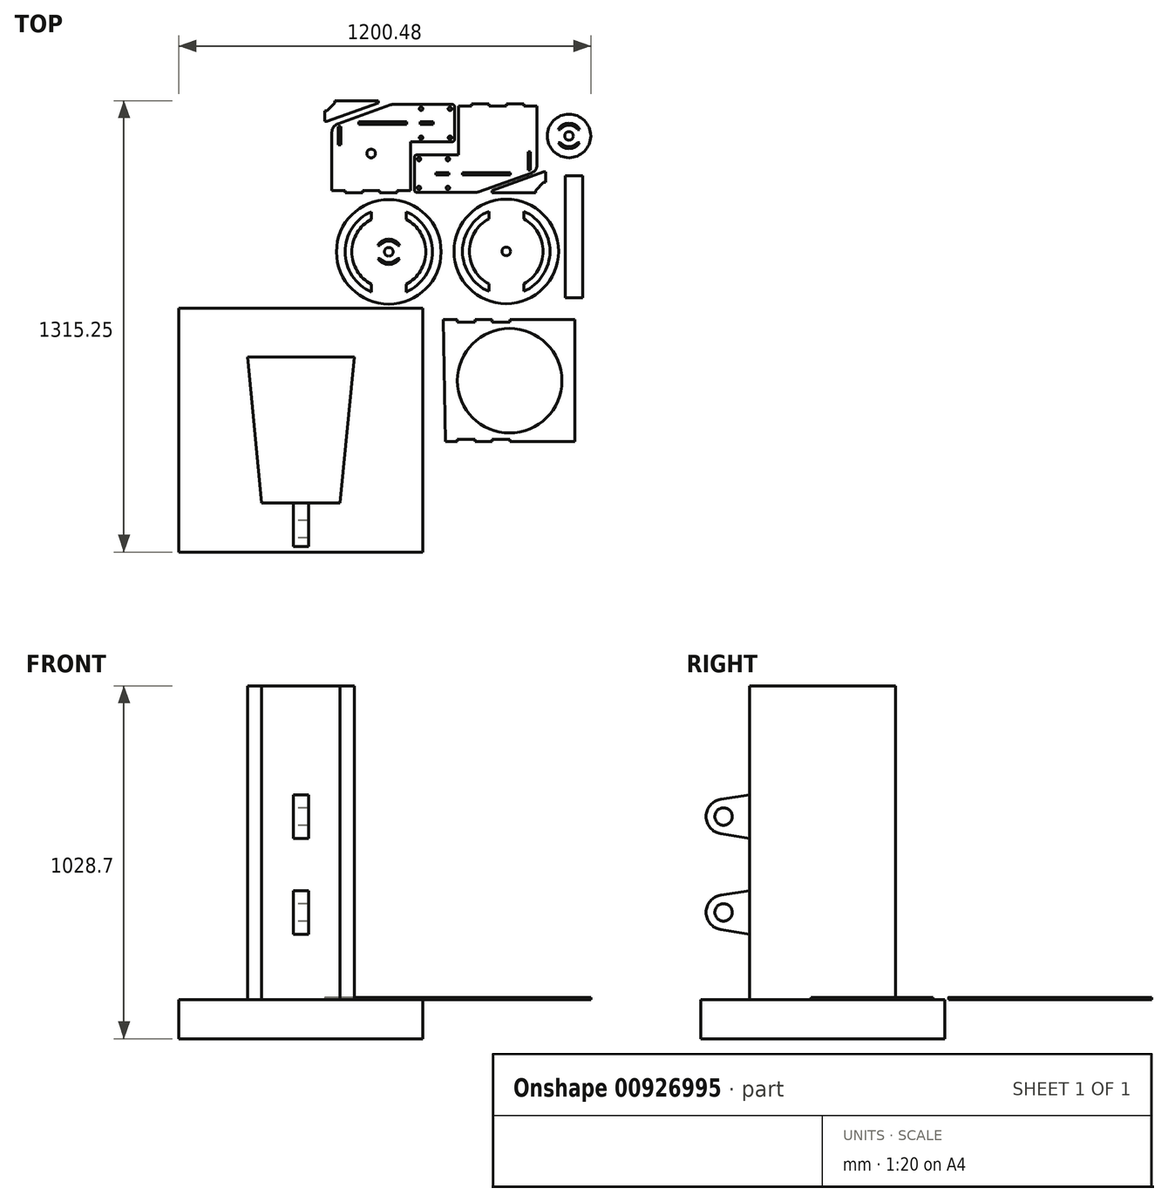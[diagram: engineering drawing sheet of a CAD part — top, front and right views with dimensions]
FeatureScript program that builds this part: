
annotation { "Feature Type Name" : "Feature", "Feature Type Description" : "" }
export const myFeature = defineFeature(function(context is Context, id is Id, definition is map)
    precondition{}
    {
        {
            var Q0;
            Q0=qCreatedBy(makeId("Top.planeOp"),FACE);
            var sketch = newSketch(context, id + "F0", { "sketchPlane" : qUnion([Q0])});
            skLineSegment(sketch, "E0", {"start": v(-368.3, -165.1) * mm, "end": v(0, -165.1) * mm});
            skLineSegment(sketch, "E1", {"start": v(101.6, -104.11) * mm, "end": v(101.6, -82.12) * mm});
            skArc(sketch, "E2", {"start": v(101.6, 107.52) * mm, "mid": v(44.83, 12.7) * mm, "end": v(101.6, -82.12) * mm});
            skArc(sketch, "E3", {"start": v(101.6, 129.51) * mm, "mid": v(25.02, 12.7) * mm, "end": v(101.6, -104.11) * mm});
            skLineSegment(sketch, "E4", {"start": v(-221.48, 30.45) * mm, "end": v(-214.81, 30.45) * mm});
            skLineSegment(sketch, "E5", {"start": v(-368.3, 190.5) * mm, "end": v(0, 190.5) * mm});
            skArc(sketch, "E6", {"start": v(-158.3, 30.45) * mm, "mid": v(-189.89, 48.3) * mm, "end": v(-221.48, 30.45) * mm});
            skLineSegment(sketch, "E7", {"start": v(0, 183.9) * mm, "end": v(52.07, 183.9) * mm});
            skLineSegment(sketch, "E8", {"start": v(52.07, 183.9) * mm, "end": v(52.07, 190.5) * mm});
            skLineSegment(sketch, "E9", {"start": v(52.07, 190.5) * mm, "end": v(101.6, 190.5) * mm});
            skLineSegment(sketch, "E10", {"start": v(101.6, 190.5) * mm, "end": v(101.6, 183.9) * mm});
            skLineSegment(sketch, "E11", {"start": v(101.6, 183.9) * mm, "end": v(153.67, 183.9) * mm});
            skLineSegment(sketch, "E12", {"start": v(153.67, 183.9) * mm, "end": v(153.67, 190.5) * mm});
            skLineSegment(sketch, "E13", {"start": v(153.67, 190.5) * mm, "end": v(342.9, 190.5) * mm});
            skLineSegment(sketch, "E14", {"start": v(52.07, -165.1) * mm, "end": v(101.6, -165.1) * mm});
            skLineSegment(sketch, "E15", {"start": v(153.67, -165.1) * mm, "end": v(342.9, -165.1) * mm});
            skCircle(sketch, "E16", {"center": v(-189.89, 11.4) * mm, "radius": 152.4 * mm});
            skLineSegment(sketch, "E17", {"start": v(0, 183.9) * mm, "end": v(0, 190.5) * mm});
            skLineSegment(sketch, "E18", {"start": v(101.6, 107.52) * mm, "end": v(101.6, 129.51) * mm});
            skLineSegment(sketch, "E19", {"start": v(342.9, 190.5) * mm, "end": v(342.9, -165.1) * mm});
            skLineSegment(sketch, "E20", {"start": v(153.67, -158.5) * mm, "end": v(153.67, -165.1) * mm});
            skLineSegment(sketch, "E21", {"start": v(101.6, -158.5) * mm, "end": v(153.67, -158.5) * mm});
            skCircle(sketch, "E22", {"center": v(152.4, 12.7) * mm, "radius": 12.7 * mm});
            skLineSegment(sketch, "E23", {"start": v(101.6, -165.1) * mm, "end": v(101.6, -158.5) * mm});
            skLineSegment(sketch, "E24", {"start": v(52.07, -158.5) * mm, "end": v(52.07, -165.1) * mm});
            skLineSegment(sketch, "E25", {"start": v(0, -158.5) * mm, "end": v(52.07, -158.5) * mm});
            skLineSegment(sketch, "E26", {"start": v(0, -165.1) * mm, "end": v(0, -158.5) * mm});
            skLineSegment(sketch, "E27", {"start": v(-164.97, -7.65) * mm, "end": v(-158.3, -7.65) * mm});
            skLineSegment(sketch, "E28", {"start": v(-164.97, 30.45) * mm, "end": v(-158.3, 30.45) * mm});
            skLineSegment(sketch, "E29", {"start": v(-368.3, 190.5) * mm, "end": v(-368.3, -165.1) * mm});
            skCircle(sketch, "E30", {"center": v(-189.89, 11.4) * mm, "radius": 12.7 * mm});
            skArc(sketch, "E31", {"start": v(-164.97, 30.45) * mm, "mid": v(-189.89, 42.77) * mm, "end": v(-214.81, 30.45) * mm});
            skLineSegment(sketch, "E32", {"start": v(-221.48, -7.65) * mm, "end": v(-214.81, -7.65) * mm});
            skLineSegment(sketch, "E33", {"start": v(-139.09, 106.22) * mm, "end": v(-139.09, 128.22) * mm});
            skArc(sketch, "E34", {"start": v(-221.48, -7.65) * mm, "mid": v(-189.89, -25.5) * mm, "end": v(-158.3, -7.65) * mm});
            skArc(sketch, "E35", {"start": v(-240.69, 106.22) * mm, "mid": v(-297.46, 11.4) * mm, "end": v(-240.69, -83.42) * mm});
            skArc(sketch, "E36", {"start": v(-139.09, -83.42) * mm, "mid": v(-82.32, 11.4) * mm, "end": v(-139.09, 106.22) * mm});
            skArc(sketch, "E37", {"start": v(-240.69, 128.22) * mm, "mid": v(-317.27, 11.4) * mm, "end": v(-240.69, -105.41) * mm});
            skArc(sketch, "E38", {"start": v(-214.81, -7.65) * mm, "mid": v(-189.89, -19.97) * mm, "end": v(-164.97, -7.65) * mm});
            skLineSegment(sketch, "E39", {"start": v(-240.69, -105.41) * mm, "end": v(-240.69, -83.42) * mm});
            skLineSegment(sketch, "E40", {"start": v(-240.69, 106.22) * mm, "end": v(-240.69, 128.22) * mm});
            skLineSegment(sketch, "E41", {"start": v(-139.09, -105.41) * mm, "end": v(-139.09, -83.42) * mm});
            skCircle(sketch, "E42", {"center": v(152.4, 12.7) * mm, "radius": 152.4 * mm});
            skArc(sketch, "E43", {"start": v(-139.09, -105.41) * mm, "mid": v(-62.5, 11.4) * mm, "end": v(-139.09, 128.22) * mm});
            skLineSegment(sketch, "E44", {"start": v(203.2, 107.52) * mm, "end": v(203.2, 129.51) * mm});
            skArc(sketch, "E45", {"start": v(203.2, -82.12) * mm, "mid": v(259.97, 12.7) * mm, "end": v(203.2, 107.52) * mm});
            skArc(sketch, "E46", {"start": v(203.2, -104.11) * mm, "mid": v(279.78, 12.7) * mm, "end": v(203.2, 129.51) * mm});
            skLineSegment(sketch, "E47", {"start": v(203.2, -104.11) * mm, "end": v(203.2, -82.12) * mm});
            skSolve(sketch);
        }
        {
            var Q0;
            Q0=qCreatedBy(makeId("Top.planeOp"),FACE);
            var sketch = newSketch(context, id + "F1", { "sketchPlane" : qUnion([Q0])});
            skLineSegment(sketch, "E48", {"start": v(-119.77, 332.2) * mm, "end": v(-119.77, 441) * mm, "construction": true});
            skLineSegment(sketch, "E49", {"start": v(-336.68, 323) * mm, "end": v(-330.07, 323) * mm});
            skLineSegment(sketch, "E50", {"start": v(-336.68, 376.34) * mm, "end": v(-336.68, 323) * mm});
            skLineSegment(sketch, "E51", {"start": v(-330.07, 376.34) * mm, "end": v(-336.68, 376.34) * mm});
            skLineSegment(sketch, "E52", {"start": v(-330.07, 323) * mm, "end": v(-330.07, 376.34) * mm});
            skLineSegment(sketch, "E53", {"start": v(-277.47, 389.9) * mm, "end": v(-277.47, 383.3) * mm});
            skLineSegment(sketch, "E54", {"start": v(-137.77, 389.9) * mm, "end": v(-277.47, 389.9) * mm});
            skLineSegment(sketch, "E55", {"start": v(-137.77, 383.3) * mm, "end": v(-137.77, 389.9) * mm});
            skLineSegment(sketch, "E56", {"start": v(-277.47, 383.3) * mm, "end": v(-137.77, 383.3) * mm});
            skLineSegment(sketch, "E57", {"start": v(-127, 326.7) * mm, "end": v(-127, 190.18) * mm});
            skLineSegment(sketch, "E58", {"start": v(-127, 326.7) * mm, "end": v(-127, 332.2) * mm});
            skLineSegment(sketch, "E59", {"start": v(-127, 441) * mm, "end": v(-127, 332.2) * mm, "construction": true});
            skLineSegment(sketch, "E60", {"start": v(-176.58, 441) * mm, "end": v(-127, 441) * mm});
            skArc(sketch, "E61", {"start": v(-176.58, 441) * mm, "mid": v(-180.91, 440.64) * mm, "end": v(-185.11, 439.53) * mm});
            skLineSegment(sketch, "E62", {"start": v(-185.11, 439.53) * mm, "end": v(-338.73, 384.73) * mm});
            skArc(sketch, "E63", {"start": v(-338.73, 384.73) * mm, "mid": v(-350.96, 375.44) * mm, "end": v(-355.6, 360.8) * mm});
            skLineSegment(sketch, "E64", {"start": v(-355.6, 360.8) * mm, "end": v(-355.6, 190.18) * mm});
            skLineSegment(sketch, "E65", {"start": v(-317.5, 190.18) * mm, "end": v(-355.6, 190.18) * mm});
            skLineSegment(sketch, "E66", {"start": v(-317.5, 183.83) * mm, "end": v(-317.5, 190.18) * mm});
            skLineSegment(sketch, "E67", {"start": v(-317.5, 183.83) * mm, "end": v(-266.7, 183.83) * mm});
            skLineSegment(sketch, "E68", {"start": v(-266.7, 183.83) * mm, "end": v(-266.7, 190.18) * mm});
            skLineSegment(sketch, "E69", {"start": v(-266.7, 190.18) * mm, "end": v(-215.9, 190.18) * mm});
            skLineSegment(sketch, "E70", {"start": v(-215.9, 190.18) * mm, "end": v(-215.9, 183.83) * mm});
            skLineSegment(sketch, "E71", {"start": v(-215.9, 183.83) * mm, "end": v(-165.1, 183.83) * mm});
            skLineSegment(sketch, "E72", {"start": v(-165.1, 183.83) * mm, "end": v(-165.1, 190.18) * mm});
            skLineSegment(sketch, "E73", {"start": v(-165.1, 190.18) * mm, "end": v(-127, 190.18) * mm});
            skArc(sketch, "E74", {"start": v(-209.7, 317.18) * mm, "mid": v(-241.3, 335.03) * mm, "end": v(-272.9, 317.18) * mm});
            skLineSegment(sketch, "E75", {"start": v(-209.7, 317.18) * mm, "end": v(-216.38, 317.18) * mm});
            skArc(sketch, "E76", {"start": v(-216.38, 317.18) * mm, "mid": v(-241.3, 329.5) * mm, "end": v(-266.22, 317.18) * mm});
            skLineSegment(sketch, "E77", {"start": v(-266.22, 317.18) * mm, "end": v(-272.9, 317.18) * mm});
            skLineSegment(sketch, "E78", {"start": v(-266.22, 279.08) * mm, "end": v(-272.9, 279.08) * mm});
            skArc(sketch, "E79", {"start": v(-266.22, 279.08) * mm, "mid": v(-241.3, 266.76) * mm, "end": v(-216.38, 279.08) * mm});
            skLineSegment(sketch, "E80", {"start": v(-209.7, 279.08) * mm, "end": v(-216.38, 279.08) * mm});
            skArc(sketch, "E81", {"start": v(-272.9, 279.08) * mm, "mid": v(-241.3, 261.24) * mm, "end": v(-209.7, 279.08) * mm});
            skCircle(sketch, "E82", {"center": v(-241.3, 298.13) * mm, "radius": 12.7 * mm});
            skCircle(sketch, "E83", {"center": v(-11.6, 344.14) * mm, "radius": 5.08 * mm});
            skCircle(sketch, "E84", {"center": v(-11.6, 428.22) * mm, "radius": 5.08 * mm});
            skCircle(sketch, "E85", {"center": v(-95.68, 344.14) * mm, "radius": 5.08 * mm});
            skCircle(sketch, "E86", {"center": v(-95.68, 428.22) * mm, "radius": 5.08 * mm});
            skLineSegment(sketch, "E87", {"start": v(-112.54, 332.2) * mm, "end": v(-4.59, 332.2) * mm});
            skArc(sketch, "E88", {"start": v(-4.59, 332.2) * mm, "mid": v(-0.1, 334.07) * mm, "end": v(1.76, 338.56) * mm});
            skLineSegment(sketch, "E89", {"start": v(1.76, 338.56) * mm, "end": v(1.76, 434.66) * mm});
            skArc(sketch, "E90", {"start": v(1.76, 434.66) * mm, "mid": v(-0.1, 439.15) * mm, "end": v(-4.59, 441) * mm});
            skLineSegment(sketch, "E91", {"start": v(-4.59, 441) * mm, "end": v(-112.54, 441) * mm});
            skLineSegment(sketch, "E92", {"start": v(-112.54, 332.2) * mm, "end": v(-112.54, 441) * mm, "construction": true});
            skLineSegment(sketch, "E93", {"start": v(-60.74, 383.3) * mm, "end": v(-60.74, 389.9) * mm});
            skLineSegment(sketch, "E94", {"start": v(-98.84, 383.3) * mm, "end": v(-60.74, 383.3) * mm});
            skLineSegment(sketch, "E95", {"start": v(-98.84, 389.9) * mm, "end": v(-98.84, 383.3) * mm});
            skLineSegment(sketch, "E96", {"start": v(-60.74, 389.9) * mm, "end": v(-98.84, 389.9) * mm});
            skLineSegment(sketch, "E97", {"start": v(-127, 332.2) * mm, "end": v(-112.54, 332.2) * mm});
            skLineSegment(sketch, "E98", {"start": v(-112.54, 441) * mm, "end": v(-127, 441) * mm});
            skCircle(sketch, "E99", {"center": v(-241.3, 298.13) * mm, "radius": 63.5 * mm});
            skSolve(sketch);
        }
        {
            var Q0;
            Q0=qCreatedBy(makeId("Top.planeOp"),FACE);
            var sketch = newSketch(context, id + "F2", { "sketchPlane" : qUnion([Q0])});
            skLineSegment(sketch, "E100", {"start": v(6.33, 293.6) * mm, "end": v(6.33, 184.8) * mm, "construction": true});
            skLineSegment(sketch, "E101", {"start": v(223.24, 302.8) * mm, "end": v(216.63, 302.8) * mm});
            skLineSegment(sketch, "E102", {"start": v(223.24, 249.47) * mm, "end": v(223.24, 302.8) * mm});
            skLineSegment(sketch, "E103", {"start": v(216.63, 249.47) * mm, "end": v(223.24, 249.47) * mm});
            skLineSegment(sketch, "E104", {"start": v(216.63, 302.8) * mm, "end": v(216.63, 249.47) * mm});
            skLineSegment(sketch, "E105", {"start": v(164.04, 235.9) * mm, "end": v(164.04, 242.5) * mm});
            skLineSegment(sketch, "E106", {"start": v(24.34, 235.9) * mm, "end": v(164.04, 235.9) * mm});
            skLineSegment(sketch, "E107", {"start": v(24.34, 242.5) * mm, "end": v(24.34, 235.9) * mm});
            skLineSegment(sketch, "E108", {"start": v(164.04, 242.5) * mm, "end": v(24.34, 242.5) * mm});
            skLineSegment(sketch, "E109", {"start": v(13.56, 299.1) * mm, "end": v(13.56, 435.63) * mm});
            skLineSegment(sketch, "E110", {"start": v(13.56, 299.1) * mm, "end": v(13.56, 293.6) * mm});
            skLineSegment(sketch, "E111", {"start": v(13.56, 184.8) * mm, "end": v(13.56, 293.6) * mm, "construction": true});
            skLineSegment(sketch, "E112", {"start": v(63.14, 184.8) * mm, "end": v(13.56, 184.8) * mm});
            skArc(sketch, "E113", {"start": v(63.14, 184.8) * mm, "mid": v(67.47, 185.18) * mm, "end": v(71.68, 186.28) * mm});
            skLineSegment(sketch, "E114", {"start": v(71.68, 186.28) * mm, "end": v(225.3, 241.08) * mm});
            skArc(sketch, "E115", {"start": v(225.3, 241.08) * mm, "mid": v(237.52, 250.37) * mm, "end": v(242.16, 265) * mm});
            skLineSegment(sketch, "E116", {"start": v(242.16, 265) * mm, "end": v(242.16, 435.63) * mm});
            skLineSegment(sketch, "E117", {"start": v(204.06, 435.63) * mm, "end": v(242.16, 435.63) * mm});
            skLineSegment(sketch, "E118", {"start": v(204.06, 441.98) * mm, "end": v(204.06, 435.63) * mm});
            skLineSegment(sketch, "E119", {"start": v(204.06, 441.98) * mm, "end": v(153.26, 441.98) * mm});
            skLineSegment(sketch, "E120", {"start": v(153.26, 441.98) * mm, "end": v(153.26, 435.63) * mm});
            skLineSegment(sketch, "E121", {"start": v(153.26, 435.63) * mm, "end": v(102.46, 435.63) * mm});
            skLineSegment(sketch, "E122", {"start": v(102.46, 435.63) * mm, "end": v(102.46, 441.98) * mm});
            skLineSegment(sketch, "E123", {"start": v(102.46, 441.98) * mm, "end": v(51.66, 441.98) * mm});
            skLineSegment(sketch, "E124", {"start": v(51.66, 441.98) * mm, "end": v(51.66, 435.63) * mm});
            skLineSegment(sketch, "E125", {"start": v(51.66, 435.63) * mm, "end": v(13.56, 435.63) * mm});
            skCircle(sketch, "E126", {"center": v(-101.84, 281.67) * mm, "radius": 5.08 * mm});
            skCircle(sketch, "E127", {"center": v(-101.84, 197.6) * mm, "radius": 5.08 * mm});
            skCircle(sketch, "E128", {"center": v(-17.76, 281.67) * mm, "radius": 5.08 * mm});
            skCircle(sketch, "E129", {"center": v(-17.76, 197.6) * mm, "radius": 5.08 * mm});
            skLineSegment(sketch, "E130", {"start": v(-0.9, 293.6) * mm, "end": v(-108.85, 293.6) * mm});
            skArc(sketch, "E131", {"start": v(-108.85, 293.6) * mm, "mid": v(-113.34, 291.75) * mm, "end": v(-115.2, 287.26) * mm});
            skLineSegment(sketch, "E132", {"start": v(-115.2, 287.26) * mm, "end": v(-115.2, 191.15) * mm});
            skArc(sketch, "E133", {"start": v(-115.2, 191.15) * mm, "mid": v(-113.34, 186.66) * mm, "end": v(-108.85, 184.8) * mm});
            skLineSegment(sketch, "E134", {"start": v(-108.85, 184.8) * mm, "end": v(-0.9, 184.8) * mm});
            skLineSegment(sketch, "E135", {"start": v(-0.9, 293.6) * mm, "end": v(-0.9, 184.8) * mm, "construction": true});
            skLineSegment(sketch, "E136", {"start": v(-52.7, 242.5) * mm, "end": v(-52.7, 235.9) * mm});
            skLineSegment(sketch, "E137", {"start": v(-14.6, 242.5) * mm, "end": v(-52.7, 242.5) * mm});
            skLineSegment(sketch, "E138", {"start": v(-14.6, 235.9) * mm, "end": v(-14.6, 242.5) * mm});
            skLineSegment(sketch, "E139", {"start": v(-52.7, 235.9) * mm, "end": v(-14.6, 235.9) * mm});
            skLineSegment(sketch, "E140", {"start": v(13.56, 293.6) * mm, "end": v(-0.9, 293.6) * mm});
            skLineSegment(sketch, "E141", {"start": v(-0.9, 184.8) * mm, "end": v(13.56, 184.8) * mm});
            skSolve(sketch);
        }
        {
            var Q0;
            Q0=qCreatedBy(makeId("Top.planeOp"),FACE);
            var sketch = newSketch(context, id + "F3", { "sketchPlane" : qUnion([Q0])});
            skLineSegment(sketch, "E142", {"start": v(-370.7, 391.6) * mm, "end": v(-220.22, 445.28) * mm});
            skLineSegment(sketch, "E143", {"start": v(-220.22, 445.28) * mm, "end": v(-220.22, 451.63) * mm});
            skLineSegment(sketch, "E144", {"start": v(-347.47, 451.63) * mm, "end": v(-220.22, 451.63) * mm});
            skLineSegment(sketch, "E145", {"start": v(-347.47, 445.28) * mm, "end": v(-347.47, 451.63) * mm});
            skLineSegment(sketch, "E146", {"start": v(-347.47, 445.28) * mm, "end": v(-370.7, 422.06) * mm});
            skLineSegment(sketch, "E147", {"start": v(-370.7, 422.06) * mm, "end": v(-377.04, 422.06) * mm});
            skLineSegment(sketch, "E148", {"start": v(-377.04, 422.06) * mm, "end": v(-377.04, 391.6) * mm});
            skLineSegment(sketch, "E149", {"start": v(-370.7, 391.6) * mm, "end": v(-377.04, 391.6) * mm});
            skSolve(sketch);
        }
        {
            var Q0;
            Q0=qCreatedBy(makeId("Top.planeOp"),FACE);
            var sketch = newSketch(context, id + "F4", { "sketchPlane" : qUnion([Q0])});
            skLineSegment(sketch, "E150", {"start": v(261.09, 243.88) * mm, "end": v(110.61, 190.2) * mm});
            skLineSegment(sketch, "E151", {"start": v(110.61, 190.2) * mm, "end": v(110.61, 183.85) * mm});
            skLineSegment(sketch, "E152", {"start": v(237.87, 183.85) * mm, "end": v(110.61, 183.85) * mm});
            skLineSegment(sketch, "E153", {"start": v(237.87, 190.2) * mm, "end": v(237.87, 183.85) * mm});
            skLineSegment(sketch, "E154", {"start": v(237.87, 190.2) * mm, "end": v(261.09, 213.42) * mm});
            skLineSegment(sketch, "E155", {"start": v(261.09, 213.42) * mm, "end": v(267.44, 213.42) * mm});
            skLineSegment(sketch, "E156", {"start": v(267.44, 213.42) * mm, "end": v(267.44, 243.88) * mm});
            skLineSegment(sketch, "E157", {"start": v(261.09, 243.88) * mm, "end": v(267.44, 243.88) * mm});
            skSolve(sketch);
        }
        {
            var Q0;
            Q0=makeQuery(id+"F0.imprint","IMPRINT",FACE,{"disambiguationData":[TD([[makeQuery(id+"F0.imprint","IMPRINT",EDGE,{"derivedFrom":sQuery(id+"F0.wireOp",EDGE,"E6")}),-1.0]])]});
            var Q1;
            Q1=makeQuery(id+"F0.imprint","IMPRINT",FACE,{"disambiguationData":[TD([[makeQuery(id+"F0.imprint","IMPRINT",EDGE,{"derivedFrom":sQuery(id+"F0.wireOp",EDGE,"E1")}),-1.0]])]});
            extrude(context, id + "F5", {"entities" : qUnion([Q0, Q1]), "depth" : 6.35 * mm, "offsetDistance" : 25.4 * mm});
        }
        {
            var Q0;
            Q0 = qSketchRegion(id + "F1", true);
            var Q1;
            Q1=makeQuery(id+"F1.imprint","IMPRINT",FACE,{"disambiguationData":[TD([[makeQuery(id+"F1.imprint","IMPRINT",EDGE,{"derivedFrom":sQuery(id+"F1.wireOp",EDGE,"E74")}),-1.0]])]});
            var Q2;
            Q2=makeQuery(id+"F1.imprint","IMPRINT",FACE,{"disambiguationData":[TD([[makeQuery(id+"F1.imprint","IMPRINT",EDGE,{"derivedFrom":sQuery(id+"F1.wireOp",EDGE,"E78")}),1.0]])]});
            var Q3;
            Q3=makeQuery(id+"F1.imprint","IMPRINT",FACE,{"disambiguationData":[TD([[makeQuery(id+"F1.imprint","IMPRINT",EDGE,{"derivedFrom":sQuery(id+"F1.wireOp",EDGE,"E82")}),-1.0]])]});
            var Q4;
            Q4=makeQuery(id+"F1.imprint","IMPRINT",FACE,{"disambiguationData":[TD([[makeQuery(id+"F1.imprint","IMPRINT",EDGE,{"derivedFrom":sQuery(id+"F1.wireOp",EDGE,"E74")}),1.0]])]});
            extrude(context, id + "F6", {"entities" : qUnion([Q0, Q1, Q2, Q3, Q4]), "depth" : 6.35 * mm, "offsetDistance" : 25.4 * mm});
        }
        {
            var Q0;
            Q0=makeQuery(id+"F2.imprint","IMPRINT",FACE,{"disambiguationData":[TD([[makeQuery(id+"F2.imprint","IMPRINT",EDGE,{"derivedFrom":sQuery(id+"F2.wireOp",EDGE,"E101")}),-1.0]])]});
            extrude(context, id + "F7", {"entities" : qUnion([Q0]), "depth" : 6.35 * mm, "offsetDistance" : 25.4 * mm});
        }
        {
            var Q0;
            Q0 = qSketchRegion(id + "F3", true);
            extrude(context, id + "F8", {"entities" : qUnion([Q0]), "operationType" : NewBodyOperationType.ADD, "depth" : 6.35 * mm, "offsetDistance" : 25.4 * mm});
        }
        {
            var Q0;
            Q0 = qSketchRegion(id + "F4", true);
            extrude(context, id + "F9", {"entities" : qUnion([Q0]), "depth" : 6.35 * mm, "offsetDistance" : 25.4 * mm});
        }
        {
            var Q0;
            Q0=qCreatedBy(makeId("Top.planeOp"),FACE);
            var sketch = newSketch(context, id + "F10", { "sketchPlane" : qUnion([Q0])});
            skArc(sketch, "E158", {"start": v(366.87, 368.3) * mm, "mid": v(335.28, 386.14) * mm, "end": v(303.69, 368.3) * mm});
            skLineSegment(sketch, "E159", {"start": v(366.87, 368.3) * mm, "end": v(360.2, 368.3) * mm});
            skArc(sketch, "E160", {"start": v(360.2, 368.3) * mm, "mid": v(335.28, 380.62) * mm, "end": v(310.36, 368.3) * mm});
            skLineSegment(sketch, "E161", {"start": v(310.36, 368.3) * mm, "end": v(303.69, 368.3) * mm});
            skLineSegment(sketch, "E162", {"start": v(310.36, 330.2) * mm, "end": v(303.69, 330.2) * mm});
            skArc(sketch, "E163", {"start": v(310.36, 330.2) * mm, "mid": v(335.28, 317.88) * mm, "end": v(360.2, 330.2) * mm});
            skLineSegment(sketch, "E164", {"start": v(366.87, 330.2) * mm, "end": v(360.2, 330.2) * mm});
            skArc(sketch, "E165", {"start": v(303.69, 330.2) * mm, "mid": v(335.28, 312.36) * mm, "end": v(366.87, 330.2) * mm});
            skCircle(sketch, "E166", {"center": v(335.28, 349.25) * mm, "radius": 12.7 * mm});
            skCircle(sketch, "E167", {"center": v(335.28, 349.25) * mm, "radius": 63.5 * mm});
            skSolve(sketch);
        }
        {
            var Q0;
            Q0=makeQuery(id+"F10.imprint","IMPRINT",FACE,{"disambiguationData":[TD([[makeQuery(id+"F10.imprint","IMPRINT",EDGE,{"derivedFrom":sQuery(id+"F10.wireOp",EDGE,"E158")}),-1.0]])]});
            var Q1;
            Q1 = qConstructionFilter(qBodyType(qCreatedBy(id + "F10" ,EDGE), BodyType.WIRE), ConstructionObject.NO);
            extrude(context, id + "F11", {"entities" : qUnion([Q0]), "surfaceEntities" : qUnion([Q1]), "depth" : 6.35 * mm, "offsetDistance" : 25.4 * mm});
        }
        {
            var Q0;
            Q0=qCreatedBy(makeId("Top.planeOp"),FACE);
            var sketch = newSketch(context, id + "F12", { "sketchPlane" : qUnion([Q0])});
            skLineSegment(sketch, "E168", {"start": v(-24.67, -542.2) * mm, "end": v(9.8, -542.2) * mm});
            skLineSegment(sketch, "E169", {"start": v(111.4, -481.22) * mm, "end": v(111.4, -459.22) * mm});
            skArc(sketch, "E170", {"start": v(111.4, -269.59) * mm, "mid": v(54.64, -364.4) * mm, "end": v(111.4, -459.22) * mm});
            skArc(sketch, "E171", {"start": v(111.4, -247.6) * mm, "mid": v(34.83, -364.4) * mm, "end": v(111.4, -481.22) * mm});
            skLineSegment(sketch, "E172", {"start": v(-30.9, -186.6) * mm, "end": v(9.8, -186.6) * mm});
            skLineSegment(sketch, "E173", {"start": v(9.8, -193.2) * mm, "end": v(61.88, -193.2) * mm});
            skLineSegment(sketch, "E174", {"start": v(61.88, -193.2) * mm, "end": v(61.88, -186.6) * mm});
            skLineSegment(sketch, "E175", {"start": v(61.88, -186.6) * mm, "end": v(111.4, -186.6) * mm});
            skLineSegment(sketch, "E176", {"start": v(111.4, -186.6) * mm, "end": v(111.4, -193.2) * mm});
            skLineSegment(sketch, "E177", {"start": v(111.4, -193.2) * mm, "end": v(163.48, -193.2) * mm});
            skLineSegment(sketch, "E178", {"start": v(163.48, -193.2) * mm, "end": v(163.48, -186.6) * mm});
            skLineSegment(sketch, "E179", {"start": v(163.48, -186.6) * mm, "end": v(352.7, -186.6) * mm});
            skLineSegment(sketch, "E180", {"start": v(61.88, -542.2) * mm, "end": v(111.4, -542.2) * mm});
            skLineSegment(sketch, "E181", {"start": v(163.48, -542.2) * mm, "end": v(352.7, -542.2) * mm});
            skLineSegment(sketch, "E182", {"start": v(9.8, -193.2) * mm, "end": v(9.8, -186.6) * mm});
            skLineSegment(sketch, "E183", {"start": v(111.4, -269.59) * mm, "end": v(111.4, -247.6) * mm});
            skLineSegment(sketch, "E184", {"start": v(352.7, -186.6) * mm, "end": v(352.7, -542.2) * mm});
            skLineSegment(sketch, "E185", {"start": v(163.48, -535.6) * mm, "end": v(163.48, -542.2) * mm});
            skLineSegment(sketch, "E186", {"start": v(111.4, -535.6) * mm, "end": v(163.48, -535.6) * mm});
            skCircle(sketch, "E187", {"center": v(162.2, -364.4) * mm, "radius": 12.7 * mm});
            skLineSegment(sketch, "E188", {"start": v(111.4, -542.2) * mm, "end": v(111.4, -535.6) * mm});
            skLineSegment(sketch, "E189", {"start": v(61.88, -535.6) * mm, "end": v(61.88, -542.2) * mm});
            skLineSegment(sketch, "E190", {"start": v(9.8, -535.6) * mm, "end": v(61.88, -535.6) * mm});
            skLineSegment(sketch, "E191", {"start": v(9.8, -542.2) * mm, "end": v(9.8, -535.6) * mm});
            skCircle(sketch, "E192", {"center": v(162.2, -364.4) * mm, "radius": 152.4 * mm});
            skLineSegment(sketch, "E193", {"start": v(213, -269.59) * mm, "end": v(213, -247.6) * mm});
            skArc(sketch, "E194", {"start": v(213, -459.22) * mm, "mid": v(269.78, -364.4) * mm, "end": v(213, -269.59) * mm});
            skArc(sketch, "E195", {"start": v(213, -481.22) * mm, "mid": v(289.6, -364.4) * mm, "end": v(213, -247.6) * mm});
            skLineSegment(sketch, "E196", {"start": v(213, -481.22) * mm, "end": v(213, -459.22) * mm});
            skLineSegment(sketch, "E197", {"start": v(-30.9, -186.6) * mm, "end": v(-24.67, -542.2) * mm});
            skSolve(sketch);
        }
        {
            var Q0;
            Q0=makeQuery(id+"F12.imprint","IMPRINT",FACE,{"disambiguationData":[TD([[makeQuery(id+"F12.imprint","IMPRINT",EDGE,{"derivedFrom":sQuery(id+"F12.wireOp",EDGE,"E168")}),1.0]])]});
            extrude(context, id + "F13", {"entities" : qUnion([Q0]), "depth" : 6.35 * mm, "offsetDistance" : 25.4 * mm});
        }
        {
            var Q0;
            Q0=qCreatedBy(makeId("Top.planeOp"),FACE);
            var sketch = newSketch(context, id + "F14", { "sketchPlane" : qUnion([Q0])});
            skLineSegment(sketch, "E198", {"start": v(324.77, 232.45) * mm, "end": v(375.57, 232.45) * mm});
            skLineSegment(sketch, "E199", {"start": v(324.77, -123.15) * mm, "end": v(375.57, -123.15) * mm});
            skLineSegment(sketch, "E200", {"start": v(375.57, 232.45) * mm, "end": v(375.57, -123.15) * mm});
            skLineSegment(sketch, "E201", {"start": v(324.77, 232.45) * mm, "end": v(324.77, 115.56) * mm});
            skLineSegment(sketch, "E202.trimOffspring", {"start": v(324.77, -6.27) * mm, "end": v(324.77, -123.15) * mm});
            skLineSegment(sketch, "E203", {"start": v(324.77, 115.56) * mm, "end": v(324.77, -6.27) * mm});
            skSolve(sketch);
        }
        {
            var Q0;
            Q0=makeQuery(id+"F14.imprint","IMPRINT",FACE,{"disambiguationData":[TD([[makeQuery(id+"F14.imprint","IMPRINT",EDGE,{"derivedFrom":sQuery(id+"F14.wireOp",EDGE,"E198")}),-1.0]])]});
            extrude(context, id + "F15", {"entities" : qUnion([Q0]), "depth" : 6.35 * mm, "offsetDistance" : 25.4 * mm});
        }
        {
            var Q0;
            Q0=qCreatedBy(makeId("Top.planeOp"),FACE);
            var sketch = newSketch(context, id + "F16", { "sketchPlane" : qUnion([Q0])});
            skLineSegment(sketch, "E204", {"start": v(-560.4, -720.53) * mm, "end": v(-331.8, -720.53) * mm});
            skLineSegment(sketch, "E205", {"start": v(-331.8, -720.53) * mm, "end": v(-290.53, -295.5) * mm});
            skLineSegment(sketch, "E206", {"start": v(-290.53, -295.5) * mm, "end": v(-601.68, -295.5) * mm});
            skLineSegment(sketch, "E207", {"start": v(-601.68, -295.5) * mm, "end": v(-560.4, -720.53) * mm});
            skSolve(sketch);
        }
        {
            var Q0;
            Q0 = qSketchRegion(id + "F16", true);
            extrude(context, id + "F17", {"entities" : qUnion([Q0]), "depth" : 914.4 * mm, "offsetDistance" : 25.4 * mm});
        }
        {
            var Q0;
            Q0=makeQuery(id+"F17.opExtrude","CAP_FACE",FACE,{"disambiguationData":[OSD([sQuery(id+"F16.wireOp",EDGE,"E204"),sQuery(id+"F16.wireOp",EDGE,"E205"),sQuery(id+"F16.wireOp",EDGE,"E206"),sQuery(id+"F16.wireOp",EDGE,"E207")])],"isStart":true});
            var sketch = newSketch(context, id + "F18", { "sketchPlane" : qUnion([Q0])});
            skLineSegment(sketch, "E208.bottom", {"start": v(-90.5, 152.42) * mm, "end": v(-801.7, 152.42) * mm});
            skLineSegment(sketch, "E208.top", {"start": v(-90.5, 863.62) * mm, "end": v(-801.7, 863.62) * mm});
            skLineSegment(sketch, "E208.left", {"start": v(-90.5, 152.42) * mm, "end": v(-90.5, 863.62) * mm});
            skLineSegment(sketch, "E208.right", {"start": v(-801.7, 152.42) * mm, "end": v(-801.7, 863.62) * mm});
            skPoint(sketch, "E208.middle", {"position": v(-446.1, 508.02) * mm});
            skPoint(sketch, "E208.middle.positionSnap0", {"position": v(-446.1, 720.53) * mm});
            skPoint(sketch, "E208.centerSnap0", {"position": v(-446.1, 720.53) * mm});
            skLineSegment(sketch, "E209", {"start": v(-446.1, 720.53) * mm, "end": v(-446.1, 295.5) * mm, "construction": true});
            skSolve(sketch);
        }
        {
            var Q0;
            Q0 = qSketchRegion(id + "F18", true);
            extrude(context, id + "F19", {"entities" : qUnion([Q0]), "operationType" : NewBodyOperationType.ADD, "depth" : 114.3 * mm, "offsetDistance" : 25.4 * mm});
        }
        {
            var Q0;
            Q0=makeQuery(id+"F19.opExtrude","SWEPT_FACE",FACE,{"disambiguationData":[OSD([sQuery(id+"F18.wireOp",EDGE,"E208.left")])]});
            var Q1;
            Q1=makeQuery(id+"F19.opExtrude","SWEPT_FACE",FACE,{"disambiguationData":[OSD([sQuery(id+"F18.wireOp",EDGE,"E208.right")])]});
            cPlane(context, id + "F20", {"entities" : qUnion([Q0, Q1]), "cplaneType" : CPlaneType.MID_PLANE, "offset" : 25.4 * mm, "width" : 152.4 * mm, "height" : 152.4 * mm});
        }
        {
            var Q0;
            Q0=qCreatedBy(id+"F20.planeOp",FACE);
            var sketch = newSketch(context, id + "F21", { "sketchPlane" : qUnion([Q0])});
            skCircle(sketch, "E210", {"center": v(-796.73, 254) * mm, "radius": 25.4 * mm});
            skArc(sketch, "E211", {"start": v(-804.68, 304.17) * mm, "mid": v(-847.53, 254) * mm, "end": v(-804.68, 203.83) * mm});
            skLineSegment(sketch, "E212", {"start": v(-720.53, 317.5) * mm, "end": v(-720.53, 190.5) * mm});
            skLineSegment(sketch, "E213", {"start": v(-796.73, 254) * mm, "end": v(-720.53, 254) * mm, "construction": true});
            skPoint(sketch, "E214", {"position": v(-720.53, 254) * mm});
            skLineSegment(sketch, "E215", {"start": v(-720.53, 317.5) * mm, "end": v(-804.68, 304.17) * mm});
            skLineSegment(sketch, "E216", {"start": v(-720.53, 190.5) * mm, "end": v(-804.68, 203.83) * mm});
            skPoint(sketch, "E217", {"position": v(-847.53, 254) * mm});
            skCircle(sketch, "E218", {"center": v(-796.73, 533.4) * mm, "radius": 25.4 * mm});
            skArc(sketch, "E219", {"start": v(-804.68, 583.57) * mm, "mid": v(-847.53, 533.4) * mm, "end": v(-804.68, 483.23) * mm});
            skLineSegment(sketch, "E220", {"start": v(-720.53, 596.9) * mm, "end": v(-720.53, 469.9) * mm});
            skLineSegment(sketch, "E221", {"start": v(-796.73, 533.4) * mm, "end": v(-720.53, 533.4) * mm, "construction": true});
            skPoint(sketch, "E222", {"position": v(-720.53, 533.4) * mm});
            skLineSegment(sketch, "E223", {"start": v(-720.53, 596.9) * mm, "end": v(-804.68, 583.57) * mm});
            skLineSegment(sketch, "E224", {"start": v(-720.53, 469.9) * mm, "end": v(-804.68, 483.23) * mm});
            skPoint(sketch, "E225", {"position": v(-847.53, 533.4) * mm});
            skSolve(sketch);
        }
        {
            var Q0;
            Q0 = qSketchRegion(id + "F21", true);
            extrude(context, id + "F22", {"entities" : qUnion([Q0]), "operationType" : NewBodyOperationType.ADD, "endBound" : BoundingType.SYMMETRIC, "depth" : 44.45 * mm, "offsetDistance" : 25.4 * mm});
        }
    });
